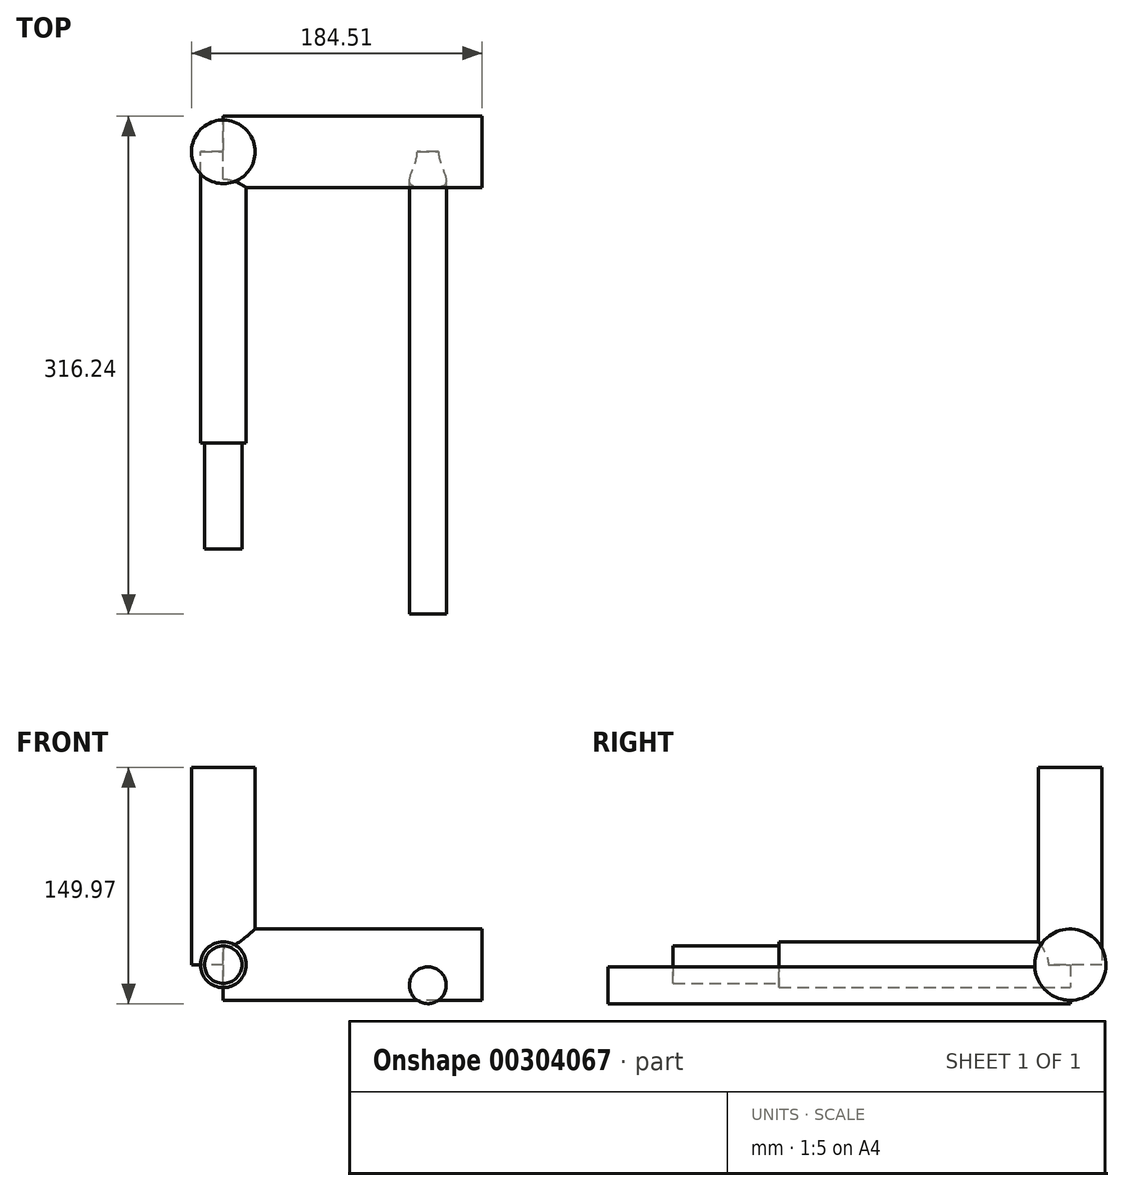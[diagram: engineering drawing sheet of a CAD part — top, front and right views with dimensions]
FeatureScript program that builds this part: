
annotation { "Feature Type Name" : "Feature", "Feature Type Description" : "" }
export const myFeature = defineFeature(function(context is Context, id is Id, definition is map)
    precondition{}
    {
        {
            var Q0;
            Q0=qCreatedBy(makeId("Right.planeOp"),FACE);
            var sketch = newSketch(context, id + "F0", { "sketchPlane" : qUnion([Q0])});
            skCircle(sketch, "E0", {"center": v(0, 0) * mm, "radius": 22.62 * mm});
            skSolve(sketch);
        }
        {
            var Q0;
            Q0 = qSketchRegion(id + "F0", true);
            extrude(context, id + "F1", {"entities" : qUnion([Q0]), "depth" : 164.34 * mm});
        }
        {
            var Q0;
            Q0=qCreatedBy(makeId("Front.planeOp"),FACE);
            var sketch = newSketch(context, id + "F2", { "sketchPlane" : qUnion([Q0])});
            skCircle(sketch, "E1", {"center": v(0, 0) * mm, "radius": 11.9 * mm});
            skSolve(sketch);
        }
        {
            var Q0;
            Q0 = qSketchRegion(id + "F2", true);
            extrude(context, id + "F3", {"entities" : qUnion([Q0]), "operationType" : NewBodyOperationType.ADD, "depth" : 252.22 * mm});
        }
        {
            var Q0;
            Q0=qCreatedBy(makeId("Front.planeOp"),FACE);
            var sketch = newSketch(context, id + "F4", { "sketchPlane" : qUnion([Q0])});
            skCircle(sketch, "E2", {"center": v(129.93, -13.06) * mm, "radius": 11.7 * mm});
            skSolve(sketch);
        }
        {
            var Q0;
            Q0 = qSketchRegion(id + "F4", true);
            extrude(context, id + "F5", {"entities" : qUnion([Q0]), "operationType" : NewBodyOperationType.ADD, "depth" : 293.62 * mm});
        }
        {
            var Q0;
            Q0=qCreatedBy(makeId("Top.planeOp"),FACE);
            var sketch = newSketch(context, id + "F6", { "sketchPlane" : qUnion([Q0])});
            skCircle(sketch, "E3", {"center": v(0, 0) * mm, "radius": 20.17 * mm});
            skSolve(sketch);
        }
        {
            var Q0;
            Q0 = qSketchRegion(id + "F6", true);
            extrude(context, id + "F7", {"entities" : qUnion([Q0]), "operationType" : NewBodyOperationType.ADD, "depth" : 125.22 * mm});
        }
        {
            var Q0;
            Q0=qCreatedBy(makeId("Front.planeOp"),FACE);
            var sketch = newSketch(context, id + "F8", { "sketchPlane" : qUnion([Q0])});
            skCircle(sketch, "E4", {"center": v(0, 0) * mm, "radius": 14.54 * mm});
            skSolve(sketch);
        }
        {
            var Q0;
            Q0 = qSketchRegion(id + "F8", true);
            extrude(context, id + "F9", {"entities" : qUnion([Q0]), "operationType" : NewBodyOperationType.ADD, "depth" : 184.9 * mm});
        }
    });
